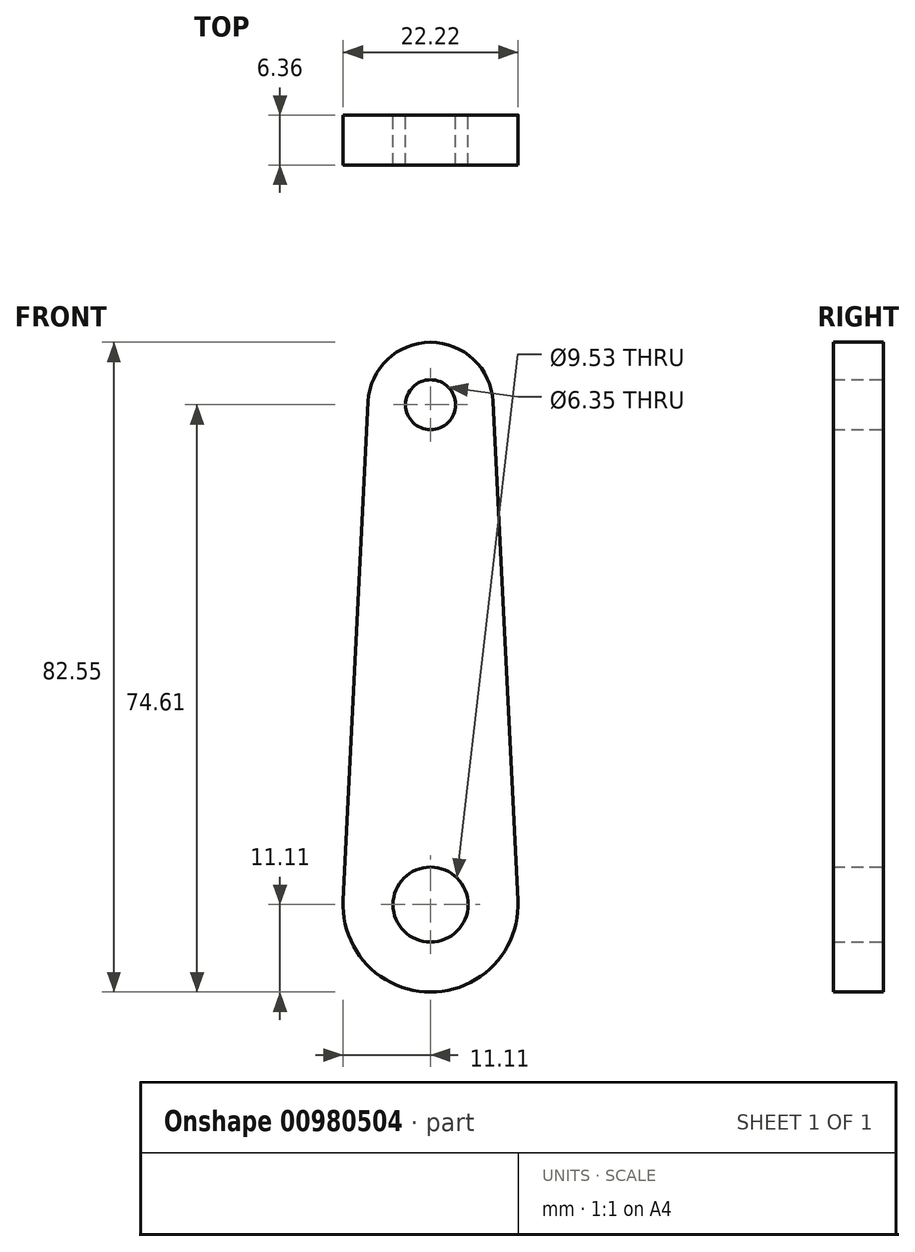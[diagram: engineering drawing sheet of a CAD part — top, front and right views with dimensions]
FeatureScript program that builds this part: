
annotation { "Feature Type Name" : "Feature", "Feature Type Description" : "" }
export const myFeature = defineFeature(function(context is Context, id is Id, definition is map)
    precondition{}
    {
        {
            var Q0;
            Q0=qCreatedBy(makeId("Front.planeOp"),FACE);
            var sketch = newSketch(context, id + "F0", { "sketchPlane" : qUnion([Q0])});
            skCircle(sketch, "E0", {"center": v(0, 0) * mm, "radius": 4.76 * mm});
            skCircle(sketch, "E1", {"center": v(0, 63.5) * mm, "radius": 3.18 * mm});
            skArc(sketch, "E2", {"start": v(7.93, 63.9) * mm, "mid": v(0, 71.44) * mm, "end": v(-7.93, 63.9) * mm});
            skArc(sketch, "E3", {"start": v(-11.1, 0.56) * mm, "mid": v(0, -11.11) * mm, "end": v(11.1, 0.56) * mm});
            skLineSegment(sketch, "E4", {"start": v(7.93, 63.9) * mm, "end": v(11.1, 0.56) * mm});
            skLineSegment(sketch, "E5", {"start": v(-11.1, 0.56) * mm, "end": v(-7.93, 63.9) * mm});
            skSolve(sketch);
        }
        {
            var Q0;
            Q0=makeQuery(id+"F0.imprint","IMPRINT",FACE,{"disambiguationData":[TD([[makeQuery(id+"F0.imprint","IMPRINT",EDGE,{"derivedFrom":sQuery(id+"F0.wireOp",EDGE,"E0")}),-1.0]])]});
            extrude(context, id + "F1", {"entities" : qUnion([Q0]), "endBound" : BoundingType.SYMMETRIC, "depth" : 6.35 * mm, "offsetDistance" : 25.4 * mm});
        }
    });
